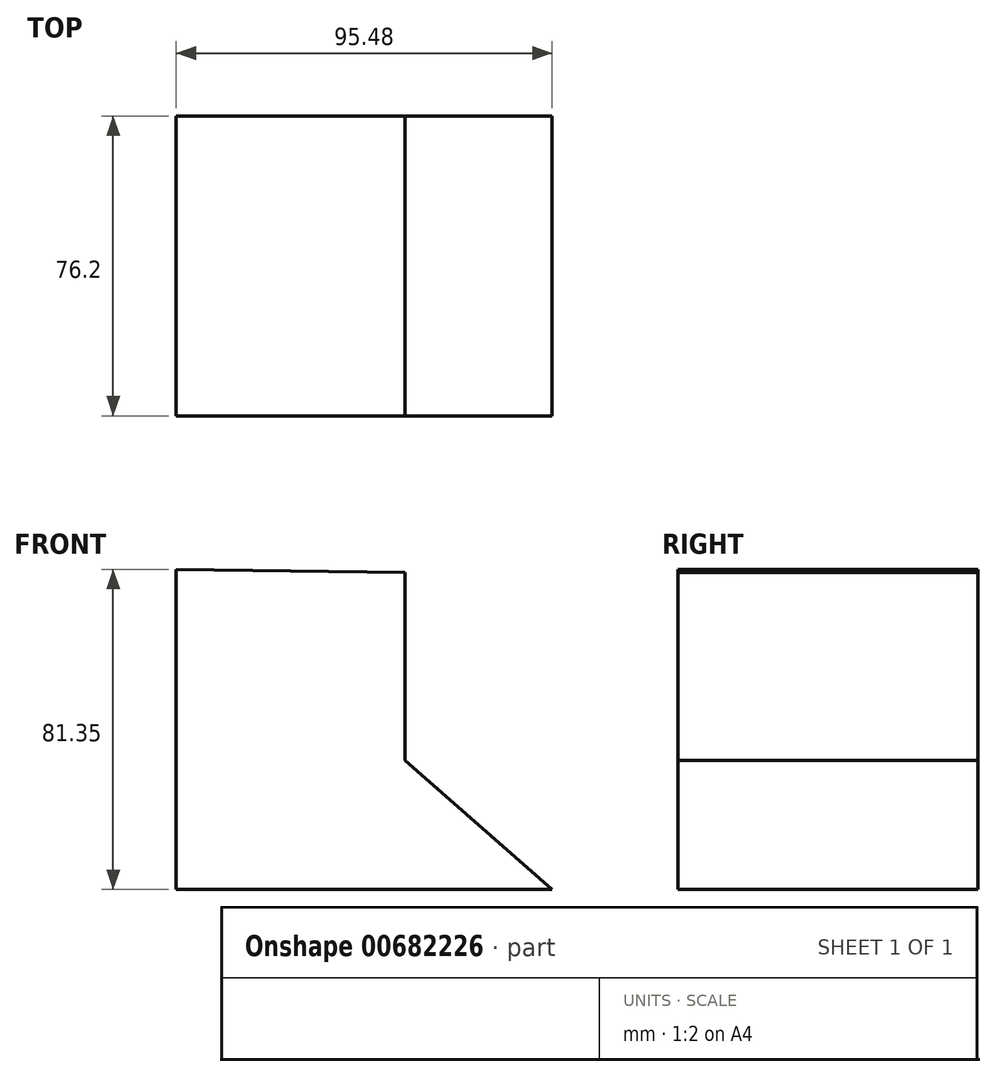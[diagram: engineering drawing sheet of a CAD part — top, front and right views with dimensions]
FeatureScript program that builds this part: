
annotation { "Feature Type Name" : "Feature", "Feature Type Description" : "" }
export const myFeature = defineFeature(function(context is Context, id is Id, definition is map)
    precondition{}
    {
        {
            var Q0;
            Q0=qCreatedBy(makeId("Front.planeOp"),FACE);
            var sketch = newSketch(context, id + "F0", { "sketchPlane" : qUnion([Q0])});
            skLineSegment(sketch, "E0", {"start": v(-58.15, 48.6) * mm, "end": v(-58.15, -32.75) * mm});
            skLineSegment(sketch, "E1", {"start": v(-58.15, -32.75) * mm, "end": v(8.88, -32.75) * mm});
            skLineSegment(sketch, "E2", {"start": v(8.88, -32.75) * mm, "end": v(37.33, -32.75) * mm});
            skLineSegment(sketch, "E3", {"start": v(37.33, -32.75) * mm, "end": v(0, 0) * mm});
            skLineSegment(sketch, "E4", {"start": v(0, 0) * mm, "end": v(0, 47.83) * mm});
            skLineSegment(sketch, "E5", {"start": v(0, 47.83) * mm, "end": v(-58.15, 48.6) * mm});
            skSolve(sketch);
        }
        {
            var Q0;
            Q0 = qSketchRegion(id + "F0", true);
            extrude(context, id + "F1", {"entities" : qUnion([Q0]), "depth" : 76.2 * mm, "offsetDistance" : 25.4 * mm});
        }
    });
